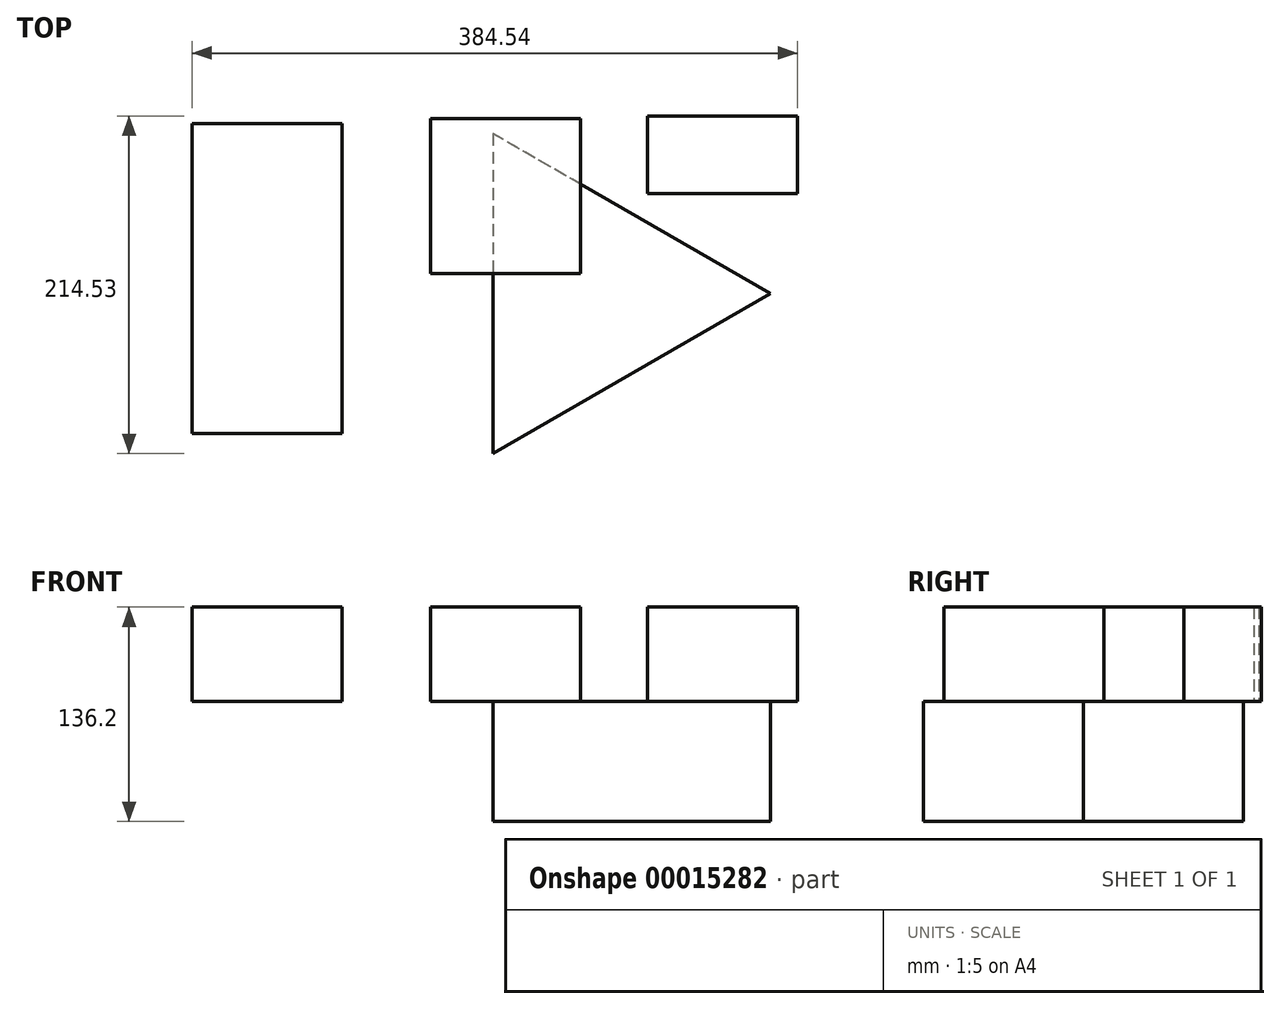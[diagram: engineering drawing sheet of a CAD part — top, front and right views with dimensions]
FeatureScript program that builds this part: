
annotation { "Feature Type Name" : "Feature", "Feature Type Description" : "" }
export const myFeature = defineFeature(function(context is Context, id is Id, definition is map)
    precondition{}
    {
        {
            var Q0;
            Q0=qCreatedBy(makeId("Top.planeOp"),FACE);
            var sketch = newSketch(context, id + "F0", { "sketchPlane" : qUnion([Q0])});
            skLineSegment(sketch, "E0.bottom", {"start": v(-191.27, 108.17) * mm, "end": v(-96.02, 108.17) * mm});
            skLineSegment(sketch, "E0.top", {"start": v(-191.27, -88.68) * mm, "end": v(-96.02, -88.68) * mm});
            skLineSegment(sketch, "E0.left", {"start": v(-191.27, 108.17) * mm, "end": v(-191.27, -88.68) * mm});
            skLineSegment(sketch, "E0.right", {"start": v(-96.02, 108.17) * mm, "end": v(-96.02, -88.68) * mm});
            skLineSegment(sketch, "E1.bottom", {"start": v(-39.94, 111.35) * mm, "end": v(55.3, 111.35) * mm});
            skLineSegment(sketch, "E1.top", {"start": v(-39.94, 12.92) * mm, "end": v(55.3, 12.92) * mm});
            skLineSegment(sketch, "E1.left", {"start": v(-39.94, 111.35) * mm, "end": v(-39.94, 12.92) * mm});
            skLineSegment(sketch, "E1.right", {"start": v(55.3, 111.35) * mm, "end": v(55.3, 12.92) * mm});
            skLineSegment(sketch, "E2.bottom", {"start": v(98.02, 112.93) * mm, "end": v(193.27, 112.93) * mm});
            skLineSegment(sketch, "E2.top", {"start": v(98.02, 63.72) * mm, "end": v(193.27, 63.72) * mm});
            skLineSegment(sketch, "E2.left", {"start": v(98.02, 112.93) * mm, "end": v(98.02, 63.72) * mm});
            skLineSegment(sketch, "E2.right", {"start": v(193.27, 112.93) * mm, "end": v(193.27, 63.72) * mm});
            skSolve(sketch);
        }
        {
            var Q0;
            Q0=makeQuery(id+"F0.imprint","IMPRINT",FACE,{"disambiguationData":[TD([[makeQuery(id+"F0.imprint","IMPRINT",EDGE,{"derivedFrom":sQuery(id+"F0.wireOp",EDGE,"E0.bottom")}),-1.0]])]});
            var Q1;
            Q1=makeQuery(id+"F0.imprint","IMPRINT",FACE,{"disambiguationData":[TD([[makeQuery(id+"F0.imprint","IMPRINT",EDGE,{"derivedFrom":sQuery(id+"F0.wireOp",EDGE,"E1.bottom")}),-1.0]])]});
            var Q2;
            Q2=makeQuery(id+"F0.imprint","IMPRINT",FACE,{"disambiguationData":[TD([[makeQuery(id+"F0.imprint","IMPRINT",EDGE,{"derivedFrom":sQuery(id+"F0.wireOp",EDGE,"E2.bottom")}),-1.0]])]});
            extrude(context, id + "F1", {"entities" : qUnion([Q0, Q1, Q2]), "depth" : 60 * mm});
        }
        {
            var Q0;
            Q0=qCreatedBy(makeId("Top.planeOp"),FACE);
            var sketch = newSketch(context, id + "F2", { "sketchPlane" : qUnion([Q0])});
            skLineSegment(sketch, "E3", {"start": v(0, 101.6) * mm, "end": v(0, -101.6) * mm});
            skLineSegment(sketch, "E4", {"start": v(0, -101.6) * mm, "end": v(175.98, 0) * mm});
            skLineSegment(sketch, "E5", {"start": v(175.98, 0) * mm, "end": v(0, 101.6) * mm});
            skSolve(sketch);
        }
        {
            var Q0;
            Q0=makeQuery(id+"F2.imprint","IMPRINT",FACE,{"disambiguationData":[TD([[makeQuery(id+"F2.imprint","IMPRINT",EDGE,{"derivedFrom":sQuery(id+"F2.wireOp",EDGE,"E3")}),1.0]])]});
            extrude(context, id + "F3", {"entities" : qUnion([Q0]), "oppositeDirection" : true, "depth" : 76.2 * mm});
        }
    });
